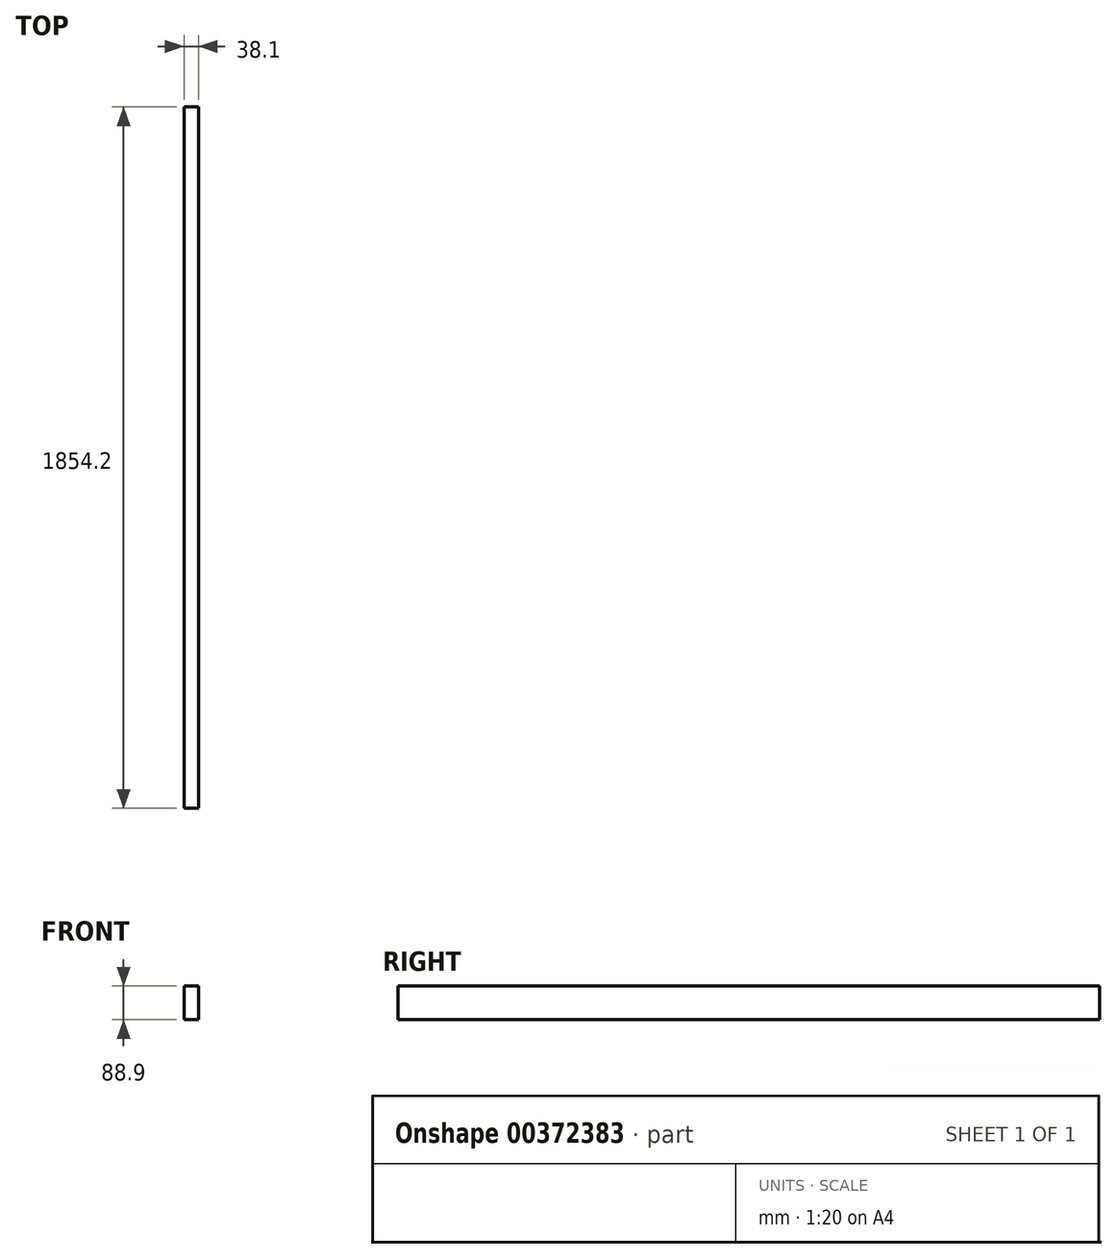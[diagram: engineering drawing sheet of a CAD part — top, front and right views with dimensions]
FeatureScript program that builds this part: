
annotation { "Feature Type Name" : "Feature", "Feature Type Description" : "" }
export const myFeature = defineFeature(function(context is Context, id is Id, definition is map)
    precondition{}
    {
        {
            var Q0;
            Q0=qCreatedBy(makeId("Front.planeOp"),FACE);
            var sketch = newSketch(context, id + "F0", { "sketchPlane" : qUnion([Q0])});
            skLineSegment(sketch, "E0.bottom", {"start": v(-19.05, 44.45) * mm, "end": v(19.05, 44.45) * mm});
            skLineSegment(sketch, "E0.top", {"start": v(-19.05, -44.45) * mm, "end": v(19.05, -44.45) * mm});
            skLineSegment(sketch, "E0.left", {"start": v(-19.05, 44.45) * mm, "end": v(-19.05, -44.45) * mm});
            skLineSegment(sketch, "E0.right", {"start": v(19.05, 44.45) * mm, "end": v(19.05, -44.45) * mm});
            skPoint(sketch, "E0.middle", {"position": v(0, 0) * mm});
            skSolve(sketch);
        }
        {
            var Q0;
            Q0=qSketchRegion(id+"F0",true);
            extrude(context, id + "F1", {"entities" : qUnion([Q0]), "endBound" : BoundingType.SYMMETRIC, "oppositeDirection" : true, "depth" : 1854.2 * mm});
        }
    });
